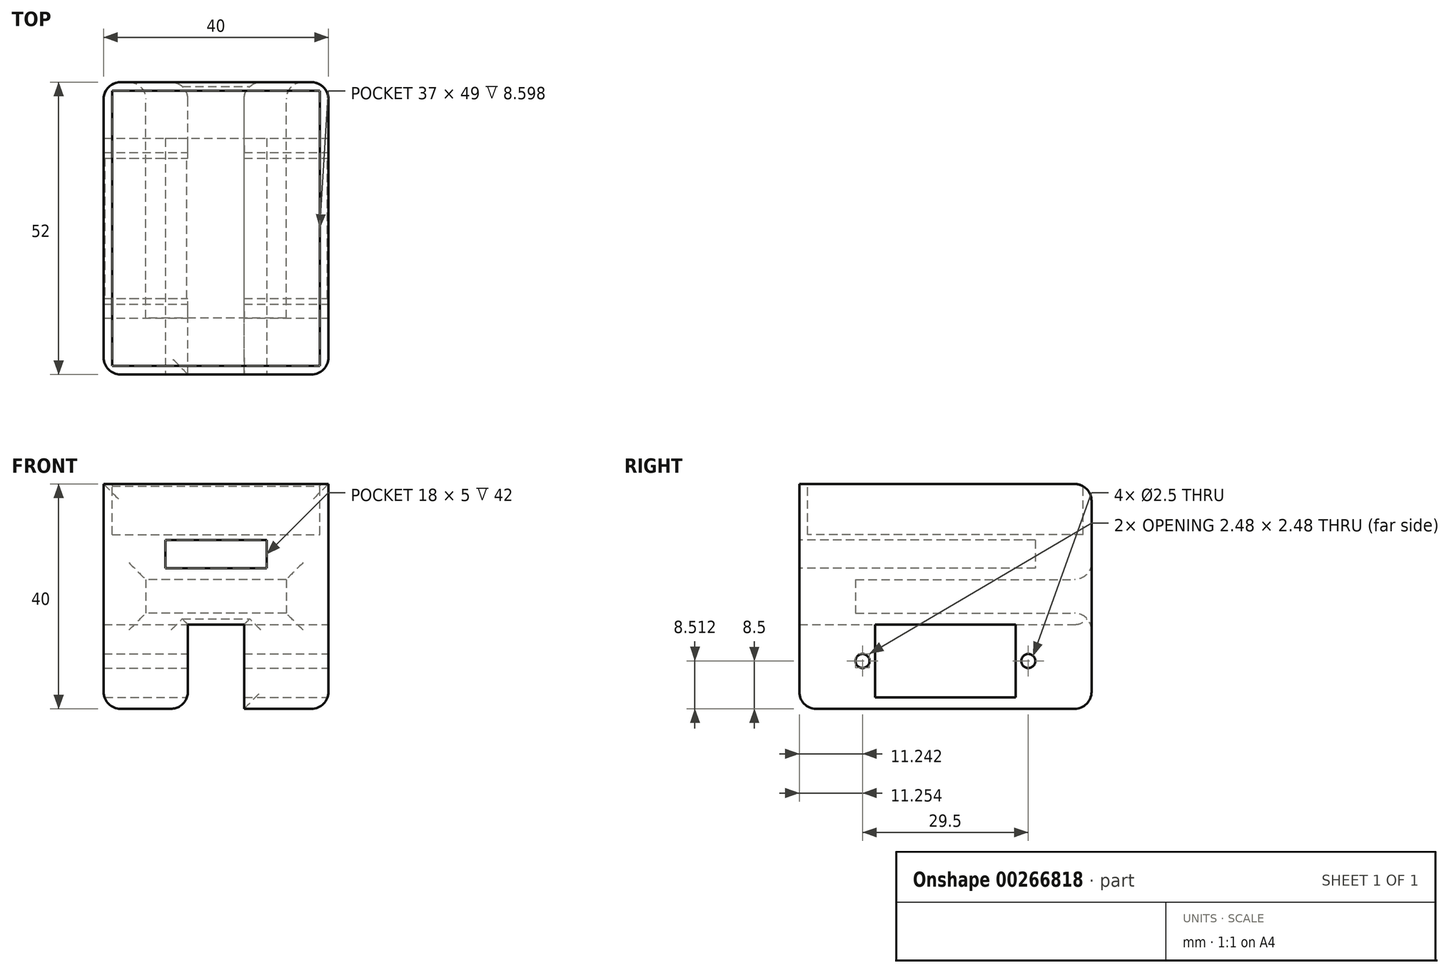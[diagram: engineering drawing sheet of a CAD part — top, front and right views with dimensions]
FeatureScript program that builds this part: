
annotation { "Feature Type Name" : "Feature", "Feature Type Description" : "" }
export const myFeature = defineFeature(function(context is Context, id is Id, definition is map)
    precondition{}
    {
        {
            var Q0;
            Q0=qCreatedBy(makeId("Top.planeOp"),FACE);
            var sketch = newSketch(context, id + "F0", { "sketchPlane" : qUnion([Q0])});
            skLineSegment(sketch, "E0.bottom", {"start": v(-10.07, -20.47) * mm, "end": v(29.93, -20.47) * mm});
            skLineSegment(sketch, "E0.top", {"start": v(-10.07, 31.53) * mm, "end": v(29.93, 31.53) * mm});
            skLineSegment(sketch, "E0.left", {"start": v(-10.07, -20.47) * mm, "end": v(-10.07, 31.53) * mm});
            skLineSegment(sketch, "E0.right", {"start": v(29.93, -20.47) * mm, "end": v(29.93, 31.53) * mm});
            skSolve(sketch);
        }
        {
            var Q0;
            Q0 = qSketchRegion(id + "F0", true);
            extrude(context, id + "F1", {"entities" : qUnion([Q0]), "depth" : 40 * mm, "offsetDistance" : 25 * mm});
        }
        {
            var Q0;
            Q0=makeQuery(id+"F1.opExtrude","SWEPT_FACE",FACE,{"disambiguationData":[OSD([sQuery(id+"F0.wireOp",EDGE,"E0.right")])]});
            var sketch = newSketch(context, id + "F2", { "sketchPlane" : qUnion([Q0])});
            skLineSegment(sketch, "E1.bottom", {"start": v(-6.97, 15) * mm, "end": v(18.03, 15) * mm});
            skLineSegment(sketch, "E1.top", {"start": v(-6.97, 2) * mm, "end": v(18.03, 2) * mm});
            skLineSegment(sketch, "E1.left", {"start": v(-6.97, 15) * mm, "end": v(-6.97, 2) * mm});
            skLineSegment(sketch, "E1.right", {"start": v(18.03, 15) * mm, "end": v(18.03, 2) * mm});
            skCircle(sketch, "E2", {"center": v(-9.22, 8.5) * mm, "radius": 1.25 * mm});
            skPoint(sketch, "E2.centerSnap0", {"position": v(-6.97, 8.5) * mm});
            skCircle(sketch, "E3", {"center": v(20.28, 8.5) * mm, "radius": 1.25 * mm});
            skSolve(sketch);
        }
        {
            var Q0;
            Q0 = qSketchRegion(id + "F2", true);
            extrude(context, id + "F3", {"entities" : qUnion([Q0]), "operationType" : NewBodyOperationType.REMOVE, "endBound" : BoundingType.THROUGH_ALL, "oppositeDirection" : true, "depth" : 25 * mm, "offsetDistance" : 25 * mm});
        }
        {
            var Q0;
            Q0=makeQuery(id+"F1.opExtrude","CAP_FACE",FACE,{"disambiguationData":[OSD([sQuery(id+"F0.wireOp",EDGE,"E0.bottom"),sQuery(id+"F0.wireOp",EDGE,"E0.top"),sQuery(id+"F0.wireOp",EDGE,"E0.left"),sQuery(id+"F0.wireOp",EDGE,"E0.right")])],"isStart":true});
            var sketch = newSketch(context, id + "F4", { "sketchPlane" : qUnion([Q0])});
            skLineSegment(sketch, "E4.bottom", {"start": v(4.93, 20.47) * mm, "end": v(14.93, 20.47) * mm});
            skLineSegment(sketch, "E4.top", {"start": v(4.93, -31.53) * mm, "end": v(14.93, -31.53) * mm});
            skLineSegment(sketch, "E4.left", {"start": v(4.93, 20.47) * mm, "end": v(4.93, -31.53) * mm});
            skLineSegment(sketch, "E4.right", {"start": v(14.93, 20.47) * mm, "end": v(14.93, -31.53) * mm});
            skSolve(sketch);
        }
        {
            var Q0;
            Q0 = qSketchRegion(id + "F4", true);
            extrude(context, id + "F5", {"entities" : qUnion([Q0]), "operationType" : NewBodyOperationType.REMOVE, "oppositeDirection" : true, "depth" : 15 * mm, "offsetDistance" : 25 * mm});
        }
        {
            var Q0;
            Q0=makeQuery(id+"F1.opExtrude","SWEPT_FACE",FACE,{"disambiguationData":[OSD([sQuery(id+"F0.wireOp",EDGE,"E0.top")])]});
            var sketch = newSketch(context, id + "F6", { "sketchPlane" : qUnion([Q0])});
            skLineSegment(sketch, "E5.bottom", {"start": v(-22.43, 23) * mm, "end": v(2.57, 23) * mm});
            skLineSegment(sketch, "E5.top", {"start": v(-22.43, 17) * mm, "end": v(2.57, 17) * mm});
            skLineSegment(sketch, "E5.left", {"start": v(-22.43, 23) * mm, "end": v(-22.43, 17) * mm});
            skLineSegment(sketch, "E5.right", {"start": v(2.57, 23) * mm, "end": v(2.57, 17) * mm});
            skSolve(sketch);
        }
        {
            var Q0;
            Q0 = qSketchRegion(id + "F6", true);
            extrude(context, id + "F7", {"entities" : qUnion([Q0]), "operationType" : NewBodyOperationType.REMOVE, "oppositeDirection" : true, "depth" : 42 * mm, "offsetDistance" : 25 * mm});
        }
        {
            var Q0;
            Q0=makeQuery(id+"F1.opExtrude","SWEPT_FACE",FACE,{"disambiguationData":[OSD([sQuery(id+"F0.wireOp",EDGE,"E0.bottom")])]});
            var sketch = newSketch(context, id + "F8", { "sketchPlane" : qUnion([Q0])});
            skLineSegment(sketch, "E6.bottom", {"start": v(0.93, 30) * mm, "end": v(18.93, 30) * mm});
            skLineSegment(sketch, "E6.top", {"start": v(0.93, 25) * mm, "end": v(18.93, 25) * mm});
            skLineSegment(sketch, "E6.left", {"start": v(0.93, 30) * mm, "end": v(0.93, 25) * mm});
            skLineSegment(sketch, "E6.right", {"start": v(18.93, 30) * mm, "end": v(18.93, 25) * mm});
            skSolve(sketch);
        }
        {
            var Q0;
            Q0 = qSketchRegion(id + "F8", true);
            extrude(context, id + "F9", {"entities" : qUnion([Q0]), "operationType" : NewBodyOperationType.REMOVE, "oppositeDirection" : true, "depth" : 42 * mm, "offsetDistance" : 25 * mm});
        }
        {
            var Q0;
            Q0=makeQuery(id+"F1.opExtrude","CAP_FACE",FACE,{"disambiguationData":[OSD([sQuery(id+"F0.wireOp",EDGE,"E0.bottom"),sQuery(id+"F0.wireOp",EDGE,"E0.top"),sQuery(id+"F0.wireOp",EDGE,"E0.left"),sQuery(id+"F0.wireOp",EDGE,"E0.right")])],"isStart":false});
            var sketch = newSketch(context, id + "F10", { "sketchPlane" : qUnion([Q0])});
            skLineSegment(sketch, "E7.bottom", {"start": v(-8.57, 30.03) * mm, "end": v(28.43, 30.03) * mm});
            skLineSegment(sketch, "E7.top", {"start": v(-8.57, -18.97) * mm, "end": v(28.43, -18.97) * mm});
            skLineSegment(sketch, "E7.left", {"start": v(-8.57, 30.03) * mm, "end": v(-8.57, -18.97) * mm});
            skLineSegment(sketch, "E7.right", {"start": v(28.43, 30.03) * mm, "end": v(28.43, -18.97) * mm});
            skSolve(sketch);
        }
        {
            var Q0;
            Q0 = qSketchRegion(id + "F10", true);
            extrude(context, id + "F11", {"entities" : qUnion([Q0]), "operationType" : NewBodyOperationType.REMOVE, "oppositeDirection" : true, "depth" : 9 * mm, "offsetDistance" : 25 * mm});
        }
        {
            var Q0;
            Q0=makeQuery(id+"F1.opExtrude","SWEPT_EDGE",EDGE,{"disambiguationData":[OSD([sQuery(id+"F0.wireOp",EDGE,"E0.bottom"),sQuery(id+"F0.wireOp",EDGE,"E0.left")])]});
            var Q1;
            Q1=makeQuery(id+"F1.opExtrude","SWEPT_EDGE",EDGE,{"disambiguationData":[OSD([sQuery(id+"F0.wireOp",EDGE,"E0.bottom"),sQuery(id+"F0.wireOp",EDGE,"E0.right")])]});
            var Q2;
            Q2=makeQuery(id+"F1.opExtrude","SWEPT_EDGE",EDGE,{"disambiguationData":[OSD([sQuery(id+"F0.wireOp",EDGE,"E0.top"),sQuery(id+"F0.wireOp",EDGE,"E0.left")])]});
            var Q3;
            Q3=makeQuery(id+"F1.opExtrude","SWEPT_EDGE",EDGE,{"disambiguationData":[OSD([sQuery(id+"F0.wireOp",EDGE,"E0.top"),sQuery(id+"F0.wireOp",EDGE,"E0.right")])]});
            var Q4;
            Q4=makeQuery(id+"F7.boolean.opBoolean","COPY",EDGE,{"derivedFrom":makeQuery(id+"F7.opExtrude","CAP_EDGE",EDGE,{"disambiguationData":[OSD([sQuery(id+"F6.wireOp",EDGE,"E5.top")])],"isStart":true})});
            var Q5;
            Q5=makeQuery(id+"F1.opExtrude","SWEPT_FACE",FACE,{"disambiguationData":[OSD([sQuery(id+"F0.wireOp",EDGE,"E0.top")])]});
            var Q6;
            Q6=makeQuery(id+"F9.boolean.opBoolean","COPY",EDGE,{"derivedFrom":makeQuery(id+"F9.opExtrude","CAP_EDGE",EDGE,{"disambiguationData":[OSD([sQuery(id+"F8.wireOp",EDGE,"E6.right")])],"isStart":true})});
            var Q7;
            Q7=makeQuery(id+"F9.boolean.opBoolean","COPY",EDGE,{"derivedFrom":makeQuery(id+"F9.opExtrude","CAP_EDGE",EDGE,{"disambiguationData":[OSD([sQuery(id+"F8.wireOp",EDGE,"E6.bottom")])],"isStart":true})});
            var Q8;
            Q8=makeQuery(id+"F9.boolean.opBoolean","COPY",EDGE,{"derivedFrom":makeQuery(id+"F9.opExtrude","CAP_EDGE",EDGE,{"disambiguationData":[OSD([sQuery(id+"F8.wireOp",EDGE,"E6.left")])],"isStart":true})});
            var Q9;
            Q9=makeQuery(id+"F9.boolean.opBoolean","COPY",EDGE,{"derivedFrom":makeQuery(id+"F9.opExtrude","CAP_EDGE",EDGE,{"disambiguationData":[OSD([sQuery(id+"F8.wireOp",EDGE,"E6.top")])],"isStart":true})});
            var Q10;
            {var subQ0=sQuery(id+"F0.wireOp",EDGE,"E0.bottom");var subQ1=sQuery(id+"F0.wireOp",EDGE,"E0.right");Q10=makeQuery(id+"F5.boolean.opBoolean","SPLIT",EDGE,{"disambiguationData":[TD([makeQuery(id+"F1.opExtrude","SWEPT_FACE",FACE,{"disambiguationData":[OSD([subQ1])]})])],"derivedFrom":makeQuery(id+"F1.opExtrude","CAP_EDGE",EDGE,{"disambiguationData":[OSD([subQ0])],"isStart":true})});}
            var Q11;
            {var subQ0=sQuery(id+"F0.wireOp",EDGE,"E0.bottom");var subQ1=sQuery(id+"F0.wireOp",EDGE,"E0.left");Q11=makeQuery(id+"F5.boolean.opBoolean","SPLIT",EDGE,{"disambiguationData":[TD([makeQuery(id+"F1.opExtrude","SWEPT_FACE",FACE,{"disambiguationData":[OSD([subQ1])]})])],"derivedFrom":makeQuery(id+"F1.opExtrude","CAP_EDGE",EDGE,{"disambiguationData":[OSD([subQ0])],"isStart":true})});}
            var Q12;
            Q12=makeQuery(id+"F1.opExtrude","CAP_EDGE",EDGE,{"disambiguationData":[OSD([sQuery(id+"F0.wireOp",EDGE,"E0.left")])],"isStart":true});
            var Q13;
            Q13=makeQuery(id+"F1.opExtrude","CAP_EDGE",EDGE,{"disambiguationData":[OSD([sQuery(id+"F0.wireOp",EDGE,"E0.right")])],"isStart":true});
            var Q14;
            Q14=makeQuery(id+"F5.boolean.opBoolean","COPY",EDGE,{"derivedFrom":makeQuery(id+"F5.opExtrude","CAP_EDGE",EDGE,{"disambiguationData":[OSD([sQuery(id+"F4.wireOp",EDGE,"E4.left")])],"isStart":true})});
            var Q15;
            Q15=makeQuery(id+"F5.boolean.opBoolean","COPY",EDGE,{"derivedFrom":makeQuery(id+"F5.opExtrude","CAP_EDGE",EDGE,{"disambiguationData":[OSD([sQuery(id+"F4.wireOp",EDGE,"E4.right")])],"isStart":true})});
            var Q16;
            Q16=makeQuery(id+"F5.boolean.opBoolean","COPY",EDGE,{"derivedFrom":makeQuery(id+"F5.opExtrude","SWEPT_EDGE",EDGE,{"disambiguationData":[OSD([sQuery(id+"F0.wireOp",EDGE,"E0.bottom"),sQuery(id+"F4.wireOp",EDGE,"E4.bottom"),sQuery(id+"F4.wireOp",EDGE,"E4.left")])]})});
            var Q17;
            Q17=makeQuery(id+"F5.boolean.opBoolean","COPY",EDGE,{"derivedFrom":makeQuery(id+"F5.opExtrude","SWEPT_EDGE",EDGE,{"disambiguationData":[OSD([sQuery(id+"F0.wireOp",EDGE,"E0.bottom"),sQuery(id+"F4.wireOp",EDGE,"E4.bottom"),sQuery(id+"F4.wireOp",EDGE,"E4.right")])]})});
            fillet(context, id + "F12", {"entities" : qUnion([Q0, Q1, Q2, Q3, Q4, Q5, Q6, Q7, Q8, Q9, Q10, Q11, Q12, Q13, Q14, Q15, Q16, Q17]), "radius" : 3 * mm, "tangentPropagation" : true, "allowEdgeOverflow" : false});
        }
    });
